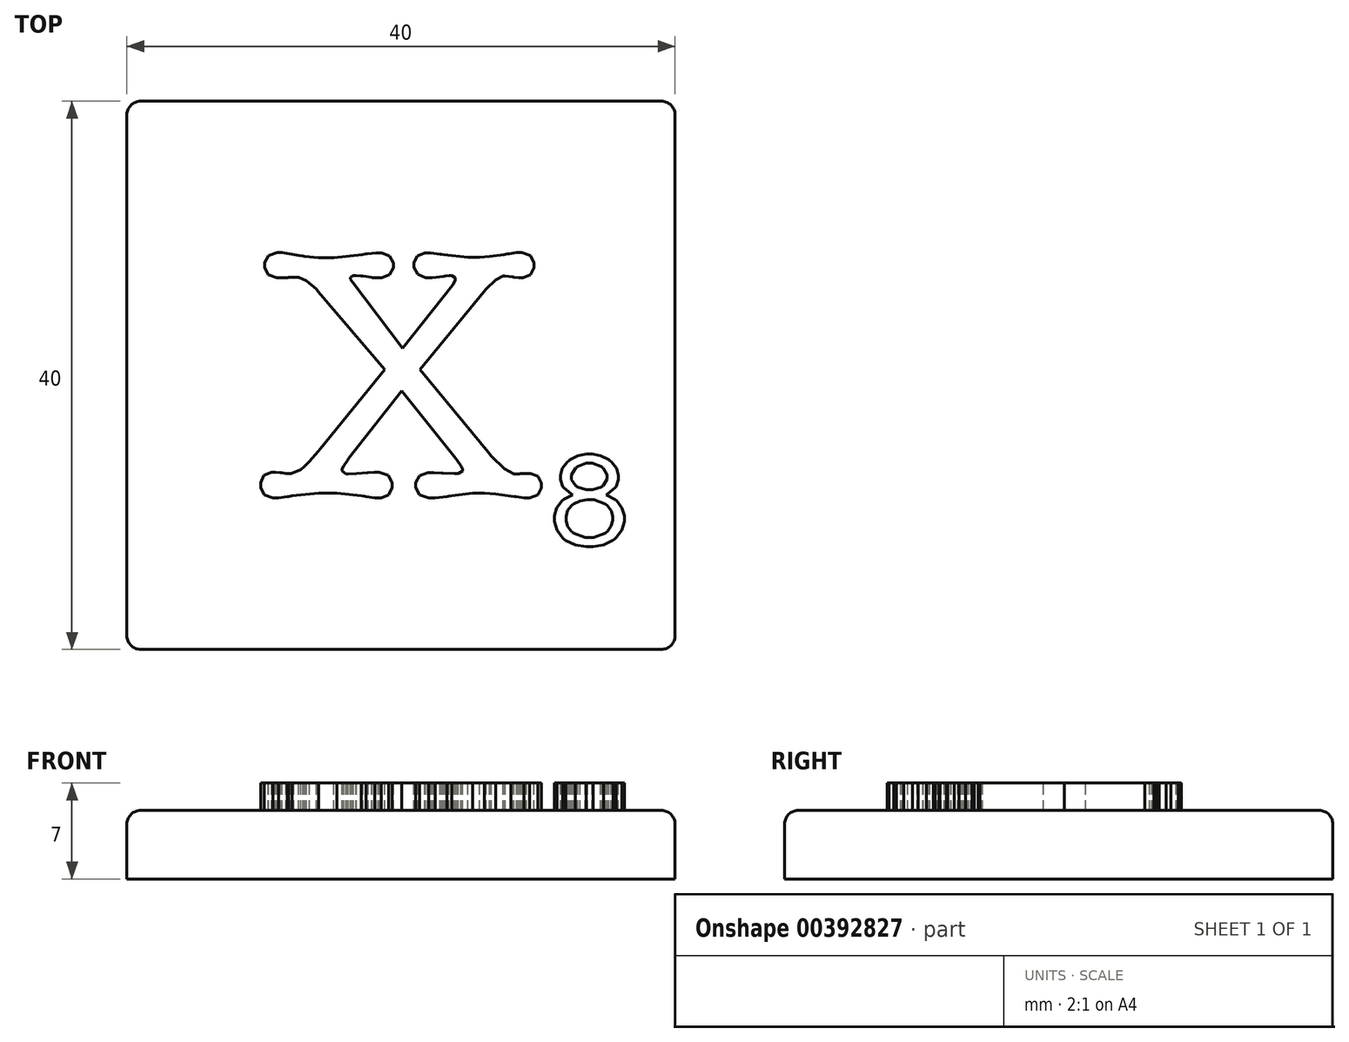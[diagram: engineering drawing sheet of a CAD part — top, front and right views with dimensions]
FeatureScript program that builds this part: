
annotation { "Feature Type Name" : "Feature", "Feature Type Description" : "" }
export const myFeature = defineFeature(function(context is Context, id is Id, definition is map)
    precondition{}
    {
        {
            var Q0;
            Q0=qCreatedBy(makeId("Top.planeOp"),FACE);
            var sketch = newSketch(context, id + "F0", { "sketchPlane" : qUnion([Q0])});
            skLineSegment(sketch, "E0.bottom", {"start": v(20, -20) * mm, "end": v(-20, -20) * mm});
            skLineSegment(sketch, "E0.top", {"start": v(20, 20) * mm, "end": v(-20, 20) * mm});
            skLineSegment(sketch, "E0.left", {"start": v(20, -20) * mm, "end": v(20, 20) * mm});
            skLineSegment(sketch, "E0.right", {"start": v(-20, -20) * mm, "end": v(-20, 20) * mm});
            skPoint(sketch, "E0.middle", {"position": v(0, 0) * mm});
            skSolve(sketch);
        }
        {
            var Q0;
            Q0=makeQuery(id+"F0.imprint","IMPRINT",FACE,{"disambiguationData":[TD([[makeQuery(id+"F0.imprint","IMPRINT",EDGE,{"derivedFrom":sQuery(id+"F0.wireOp",EDGE,"E0.bottom")}),-1.0]])]});
            extrude(context, id + "F1", {"entities" : qUnion([Q0]), "depth" : -5 * mm});
        }
        {
            var Q0;
            Q0=makeQuery(id+"F1.opExtrude","CAP_FACE",FACE,{"disambiguationData":[OSD([sQuery(id+"F0.wireOp",EDGE,"E0.bottom"),sQuery(id+"F0.wireOp",EDGE,"E0.top"),sQuery(id+"F0.wireOp",EDGE,"E0.left"),sQuery(id+"F0.wireOp",EDGE,"E0.right")])],"isStart":true});
            var Q1;
            Q1=makeQuery(id+"F1.opExtrude","SWEPT_EDGE",EDGE,{"disambiguationData":[OSD([sQuery(id+"F0.wireOp",EDGE,"E0.top"),sQuery(id+"F0.wireOp",EDGE,"E0.right")])]});
            var Q2;
            Q2=makeQuery(id+"F1.opExtrude","SWEPT_EDGE",EDGE,{"disambiguationData":[OSD([sQuery(id+"F0.wireOp",EDGE,"E0.top"),sQuery(id+"F0.wireOp",EDGE,"E0.left")])]});
            var Q3;
            Q3=makeQuery(id+"F1.opExtrude","SWEPT_EDGE",EDGE,{"disambiguationData":[OSD([sQuery(id+"F0.wireOp",EDGE,"E0.bottom"),sQuery(id+"F0.wireOp",EDGE,"E0.right")])]});
            var Q4;
            Q4=makeQuery(id+"F1.opExtrude","SWEPT_EDGE",EDGE,{"disambiguationData":[OSD([sQuery(id+"F0.wireOp",EDGE,"E0.bottom"),sQuery(id+"F0.wireOp",EDGE,"E0.left")])]});
            fillet(context, id + "F2", {"entities" : qUnion([Q0, Q1, Q2, Q3, Q4]), "radius" : 1 * mm, "tangentPropagation" : true, "allowEdgeOverflow" : false});
        }
        {
            var Q0;
            Q0=qCreatedBy(makeId("Top.planeOp"),FACE);
            var sketch = newSketch(context, id + "F3", { "sketchPlane" : qUnion([Q0])});
            skLineSegment(sketch, "E1", {"start": v(-5.87, -5.36) * mm, "end": v(-1.2, 0.41) * mm});
            skLineSegment(sketch, "E2", {"start": v(-1.2, 0.41) * mm, "end": v(-6.03, 6.1) * mm});
            skLineSegment(sketch, "E3", {"start": v(-6.03, 6.1) * mm, "end": v(-6.18, 6.28) * mm});
            skLineSegment(sketch, "E4", {"start": v(-6.18, 6.28) * mm, "end": v(-6.9, 6.9) * mm});
            skLineSegment(sketch, "E5", {"start": v(-6.9, 6.9) * mm, "end": v(-7.48, 7.16) * mm});
            skLineSegment(sketch, "E6", {"start": v(-7.48, 7.16) * mm, "end": v(-7.67, 7.16) * mm});
            skLineSegment(sketch, "E7", {"start": v(-7.67, 7.16) * mm, "end": v(-7.82, 7.16) * mm});
            skLineSegment(sketch, "E8", {"start": v(-7.82, 7.16) * mm, "end": v(-8.2, 7.14) * mm});
            skLineSegment(sketch, "E9", {"start": v(-8.2, 7.14) * mm, "end": v(-8.27, 7.13) * mm});
            skLineSegment(sketch, "E10", {"start": v(-8.27, 7.13) * mm, "end": v(-8.33, 7.13) * mm});
            skLineSegment(sketch, "E11", {"start": v(-8.33, 7.13) * mm, "end": v(-8.73, 7.1) * mm});
            skLineSegment(sketch, "E12", {"start": v(-8.73, 7.1) * mm, "end": v(-8.86, 7.1) * mm});
            skLineSegment(sketch, "E13", {"start": v(-8.86, 7.1) * mm, "end": v(-9.07, 7.1) * mm});
            skLineSegment(sketch, "E14", {"start": v(-9.07, 7.1) * mm, "end": v(-9.68, 7.34) * mm});
            skLineSegment(sketch, "E15", {"start": v(-9.68, 7.34) * mm, "end": v(-9.95, 7.88) * mm});
            skLineSegment(sketch, "E16", {"start": v(-9.95, 7.88) * mm, "end": v(-9.95, 8.06) * mm});
            skLineSegment(sketch, "E17", {"start": v(-9.95, 8.06) * mm, "end": v(-9.95, 8.23) * mm});
            skLineSegment(sketch, "E18", {"start": v(-9.95, 8.23) * mm, "end": v(-9.66, 8.73) * mm});
            skLineSegment(sketch, "E19", {"start": v(-9.66, 8.73) * mm, "end": v(-9.02, 8.96) * mm});
            skLineSegment(sketch, "E20", {"start": v(-9.02, 8.96) * mm, "end": v(-8.81, 8.96) * mm});
            skLineSegment(sketch, "E21", {"start": v(-8.81, 8.96) * mm, "end": v(-8.7, 8.96) * mm});
            skLineSegment(sketch, "E22", {"start": v(-8.7, 8.96) * mm, "end": v(-8.33, 8.89) * mm});
            skLineSegment(sketch, "E23", {"start": v(-8.33, 8.89) * mm, "end": v(-7.4, 8.74) * mm});
            skLineSegment(sketch, "E24", {"start": v(-7.4, 8.74) * mm, "end": v(-7.14, 8.7) * mm});
            skLineSegment(sketch, "E25", {"start": v(-7.14, 8.7) * mm, "end": v(-7.02, 8.67) * mm});
            skLineSegment(sketch, "E26", {"start": v(-7.02, 8.67) * mm, "end": v(-6, 8.59) * mm});
            skLineSegment(sketch, "E27", {"start": v(-6, 8.59) * mm, "end": v(-5.66, 8.59) * mm});
            skLineSegment(sketch, "E28", {"start": v(-5.66, 8.59) * mm, "end": v(-4.88, 8.59) * mm});
            skLineSegment(sketch, "E29", {"start": v(-4.88, 8.59) * mm, "end": v(-2.83, 8.8) * mm});
            skLineSegment(sketch, "E30", {"start": v(-2.83, 8.8) * mm, "end": v(-2.54, 8.85) * mm});
            skLineSegment(sketch, "E31", {"start": v(-2.54, 8.85) * mm, "end": v(-2.45, 8.86) * mm});
            skLineSegment(sketch, "E32", {"start": v(-2.45, 8.86) * mm, "end": v(-1.82, 8.93) * mm});
            skLineSegment(sketch, "E33", {"start": v(-1.82, 8.93) * mm, "end": v(-1.61, 8.93) * mm});
            skLineSegment(sketch, "E34", {"start": v(-1.61, 8.93) * mm, "end": v(-1.42, 8.93) * mm});
            skLineSegment(sketch, "E35", {"start": v(-1.42, 8.93) * mm, "end": v(-0.82, 8.7) * mm});
            skLineSegment(sketch, "E36", {"start": v(-0.82, 8.7) * mm, "end": v(-0.56, 8.2) * mm});
            skLineSegment(sketch, "E37", {"start": v(-0.56, 8.2) * mm, "end": v(-0.56, 8.03) * mm});
            skLineSegment(sketch, "E38", {"start": v(-0.56, 8.03) * mm, "end": v(-0.56, 7.86) * mm});
            skLineSegment(sketch, "E39", {"start": v(-0.56, 7.86) * mm, "end": v(-0.82, 7.34) * mm});
            skLineSegment(sketch, "E40", {"start": v(-0.82, 7.34) * mm, "end": v(-1.42, 7.1) * mm});
            skLineSegment(sketch, "E41", {"start": v(-1.42, 7.1) * mm, "end": v(-1.61, 7.1) * mm});
            skLineSegment(sketch, "E42", {"start": v(-1.61, 7.1) * mm, "end": v(-1.68, 7.1) * mm});
            skLineSegment(sketch, "E43", {"start": v(-1.68, 7.1) * mm, "end": v(-1.83, 7.13) * mm});
            skLineSegment(sketch, "E44", {"start": v(-1.83, 7.13) * mm, "end": v(-1.85, 7.13) * mm});
            skLineSegment(sketch, "E45", {"start": v(-1.85, 7.13) * mm, "end": v(-2.1, 7.13) * mm});
            skLineSegment(sketch, "E46", {"start": v(-2.1, 7.13) * mm, "end": v(-2.15, 7.14) * mm});
            skLineSegment(sketch, "E47", {"start": v(-2.15, 7.14) * mm, "end": v(-2.78, 7.23) * mm});
            skLineSegment(sketch, "E48", {"start": v(-2.78, 7.23) * mm, "end": v(-2.84, 7.24) * mm});
            skLineSegment(sketch, "E49", {"start": v(-2.84, 7.24) * mm, "end": v(-2.91, 7.25) * mm});
            skLineSegment(sketch, "E50", {"start": v(-2.91, 7.25) * mm, "end": v(-3.27, 7.29) * mm});
            skLineSegment(sketch, "E51", {"start": v(-3.27, 7.29) * mm, "end": v(-3.39, 7.29) * mm});
            skLineSegment(sketch, "E52", {"start": v(-3.39, 7.29) * mm, "end": v(-3.47, 7.29) * mm});
            skLineSegment(sketch, "E53", {"start": v(-3.47, 7.29) * mm, "end": v(-3.7, 7.15) * mm});
            skLineSegment(sketch, "E54", {"start": v(-3.7, 7.15) * mm, "end": v(-3.7, 7.1) * mm});
            skLineSegment(sketch, "E55", {"start": v(-3.7, 7.1) * mm, "end": v(-3.7, 7.03) * mm});
            skLineSegment(sketch, "E56", {"start": v(-3.7, 7.03) * mm, "end": v(-3.57, 6.82) * mm});
            skLineSegment(sketch, "E57", {"start": v(-3.57, 6.82) * mm, "end": v(-3.55, 6.79) * mm});
            skLineSegment(sketch, "E58", {"start": v(-3.55, 6.79) * mm, "end": v(0.13, 1.97) * mm});
            skLineSegment(sketch, "E59", {"start": v(0.13, 1.97) * mm, "end": v(3.76, 6.57) * mm});
            skLineSegment(sketch, "E60", {"start": v(3.76, 6.57) * mm, "end": v(3.8, 6.62) * mm});
            skLineSegment(sketch, "E61", {"start": v(3.8, 6.62) * mm, "end": v(3.97, 6.94) * mm});
            skLineSegment(sketch, "E62", {"start": v(3.97, 6.94) * mm, "end": v(3.97, 7.05) * mm});
            skLineSegment(sketch, "E63", {"start": v(3.97, 7.05) * mm, "end": v(3.97, 7.1) * mm});
            skLineSegment(sketch, "E64", {"start": v(3.97, 7.1) * mm, "end": v(3.71, 7.26) * mm});
            skLineSegment(sketch, "E65", {"start": v(3.71, 7.26) * mm, "end": v(3.62, 7.26) * mm});
            skLineSegment(sketch, "E66", {"start": v(3.62, 7.26) * mm, "end": v(3.53, 7.26) * mm});
            skLineSegment(sketch, "E67", {"start": v(3.53, 7.26) * mm, "end": v(3.26, 7.24) * mm});
            skLineSegment(sketch, "E68", {"start": v(3.26, 7.24) * mm, "end": v(3.23, 7.24) * mm});
            skLineSegment(sketch, "E69", {"start": v(3.23, 7.24) * mm, "end": v(3.1, 7.22) * mm});
            skLineSegment(sketch, "E70", {"start": v(3.1, 7.22) * mm, "end": v(2.28, 7.13) * mm});
            skLineSegment(sketch, "E71", {"start": v(2.28, 7.13) * mm, "end": v(2, 7.13) * mm});
            skLineSegment(sketch, "E72", {"start": v(2, 7.13) * mm, "end": v(1.81, 7.13) * mm});
            skLineSegment(sketch, "E73", {"start": v(1.81, 7.13) * mm, "end": v(1.22, 7.36) * mm});
            skLineSegment(sketch, "E74", {"start": v(1.22, 7.36) * mm, "end": v(0.95, 7.88) * mm});
            skLineSegment(sketch, "E75", {"start": v(0.95, 7.88) * mm, "end": v(0.95, 8.06) * mm});
            skLineSegment(sketch, "E76", {"start": v(0.95, 8.06) * mm, "end": v(0.95, 8.22) * mm});
            skLineSegment(sketch, "E77", {"start": v(0.95, 8.22) * mm, "end": v(1.2, 8.71) * mm});
            skLineSegment(sketch, "E78", {"start": v(1.2, 8.71) * mm, "end": v(1.75, 8.93) * mm});
            skLineSegment(sketch, "E79", {"start": v(1.75, 8.93) * mm, "end": v(1.93, 8.93) * mm});
            skLineSegment(sketch, "E80", {"start": v(1.93, 8.93) * mm, "end": v(2.18, 8.93) * mm});
            skLineSegment(sketch, "E81", {"start": v(2.18, 8.93) * mm, "end": v(2.83, 8.84) * mm});
            skLineSegment(sketch, "E82", {"start": v(2.83, 8.84) * mm, "end": v(2.94, 8.82) * mm});
            skLineSegment(sketch, "E83", {"start": v(2.94, 8.82) * mm, "end": v(3.14, 8.79) * mm});
            skLineSegment(sketch, "E84", {"start": v(3.14, 8.79) * mm, "end": v(4.9, 8.61) * mm});
            skLineSegment(sketch, "E85", {"start": v(4.9, 8.61) * mm, "end": v(5.48, 8.61) * mm});
            skLineSegment(sketch, "E86", {"start": v(5.48, 8.61) * mm, "end": v(5.72, 8.61) * mm});
            skLineSegment(sketch, "E87", {"start": v(5.72, 8.61) * mm, "end": v(6.46, 8.67) * mm});
            skLineSegment(sketch, "E88", {"start": v(6.46, 8.67) * mm, "end": v(7.53, 8.81) * mm});
            skLineSegment(sketch, "E89", {"start": v(7.53, 8.81) * mm, "end": v(7.78, 8.85) * mm});
            skLineSegment(sketch, "E90", {"start": v(7.78, 8.85) * mm, "end": v(7.89, 8.87) * mm});
            skLineSegment(sketch, "E91", {"start": v(7.89, 8.87) * mm, "end": v(8.44, 8.96) * mm});
            skLineSegment(sketch, "E92", {"start": v(8.44, 8.96) * mm, "end": v(8.62, 8.96) * mm});
            skLineSegment(sketch, "E93", {"start": v(8.62, 8.96) * mm, "end": v(8.83, 8.96) * mm});
            skLineSegment(sketch, "E94", {"start": v(8.83, 8.96) * mm, "end": v(9.44, 8.72) * mm});
            skLineSegment(sketch, "E95", {"start": v(9.44, 8.72) * mm, "end": v(9.71, 8.2) * mm});
            skLineSegment(sketch, "E96", {"start": v(9.71, 8.2) * mm, "end": v(9.71, 8.03) * mm});
            skLineSegment(sketch, "E97", {"start": v(9.71, 8.03) * mm, "end": v(9.71, 7.86) * mm});
            skLineSegment(sketch, "E98", {"start": v(9.71, 7.86) * mm, "end": v(9.47, 7.34) * mm});
            skLineSegment(sketch, "E99", {"start": v(9.47, 7.34) * mm, "end": v(8.91, 7.1) * mm});
            skLineSegment(sketch, "E100", {"start": v(8.91, 7.1) * mm, "end": v(8.73, 7.1) * mm});
            skLineSegment(sketch, "E101", {"start": v(8.73, 7.1) * mm, "end": v(8.6, 7.1) * mm});
            skLineSegment(sketch, "E102", {"start": v(8.6, 7.1) * mm, "end": v(8.24, 7.16) * mm});
            skLineSegment(sketch, "E103", {"start": v(8.24, 7.16) * mm, "end": v(8.18, 7.17) * mm});
            skLineSegment(sketch, "E104", {"start": v(8.18, 7.17) * mm, "end": v(8.11, 7.18) * mm});
            skLineSegment(sketch, "E105", {"start": v(8.11, 7.18) * mm, "end": v(7.62, 7.24) * mm});
            skLineSegment(sketch, "E106", {"start": v(7.62, 7.24) * mm, "end": v(7.44, 7.24) * mm});
            skLineSegment(sketch, "E107", {"start": v(7.44, 7.24) * mm, "end": v(6.91, 6.95) * mm});
            skLineSegment(sketch, "E108", {"start": v(6.91, 6.95) * mm, "end": v(6.21, 6.29) * mm});
            skLineSegment(sketch, "E109", {"start": v(6.21, 6.29) * mm, "end": v(6.06, 6.1) * mm});
            skLineSegment(sketch, "E110", {"start": v(6.06, 6.1) * mm, "end": v(1.4, 0.41) * mm});
            skLineSegment(sketch, "E111", {"start": v(1.4, 0.41) * mm, "end": v(6.38, -5.62) * mm});
            skLineSegment(sketch, "E112", {"start": v(6.38, -5.62) * mm, "end": v(6.6, -5.89) * mm});
            skLineSegment(sketch, "E113", {"start": v(6.6, -5.89) * mm, "end": v(7.55, -6.81) * mm});
            skLineSegment(sketch, "E114", {"start": v(7.55, -6.81) * mm, "end": v(8.26, -7.2) * mm});
            skLineSegment(sketch, "E115", {"start": v(8.26, -7.2) * mm, "end": v(8.5, -7.2) * mm});
            skLineSegment(sketch, "E116", {"start": v(8.5, -7.2) * mm, "end": v(8.54, -7.2) * mm});
            skLineSegment(sketch, "E117", {"start": v(8.54, -7.2) * mm, "end": v(8.66, -7.19) * mm});
            skLineSegment(sketch, "E118", {"start": v(8.66, -7.19) * mm, "end": v(8.68, -7.18) * mm});
            skLineSegment(sketch, "E119", {"start": v(8.68, -7.18) * mm, "end": v(8.84, -7.18) * mm});
            skLineSegment(sketch, "E120", {"start": v(8.84, -7.18) * mm, "end": v(8.86, -7.18) * mm});
            skLineSegment(sketch, "E121", {"start": v(8.86, -7.18) * mm, "end": v(9.16, -7.16) * mm});
            skLineSegment(sketch, "E122", {"start": v(9.16, -7.16) * mm, "end": v(9.26, -7.16) * mm});
            skLineSegment(sketch, "E123", {"start": v(9.26, -7.16) * mm, "end": v(9.44, -7.16) * mm});
            skLineSegment(sketch, "E124", {"start": v(9.44, -7.16) * mm, "end": v(10, -7.37) * mm});
            skLineSegment(sketch, "E125", {"start": v(10, -7.37) * mm, "end": v(10.24, -7.87) * mm});
            skLineSegment(sketch, "E126", {"start": v(10.24, -7.87) * mm, "end": v(10.24, -8.03) * mm});
            skLineSegment(sketch, "E127", {"start": v(10.24, -8.03) * mm, "end": v(10.24, -8.2) * mm});
            skLineSegment(sketch, "E128", {"start": v(10.24, -8.2) * mm, "end": v(9.98, -8.72) * mm});
            skLineSegment(sketch, "E129", {"start": v(9.98, -8.72) * mm, "end": v(9.4, -8.96) * mm});
            skLineSegment(sketch, "E130", {"start": v(9.4, -8.96) * mm, "end": v(9.2, -8.96) * mm});
            skLineSegment(sketch, "E131", {"start": v(9.2, -8.96) * mm, "end": v(8.98, -8.96) * mm});
            skLineSegment(sketch, "E132", {"start": v(8.98, -8.96) * mm, "end": v(8.4, -8.87) * mm});
            skLineSegment(sketch, "E133", {"start": v(8.4, -8.87) * mm, "end": v(8.28, -8.85) * mm});
            skLineSegment(sketch, "E134", {"start": v(8.28, -8.85) * mm, "end": v(8.03, -8.8) * mm});
            skLineSegment(sketch, "E135", {"start": v(8.03, -8.8) * mm, "end": v(6.91, -8.67) * mm});
            skLineSegment(sketch, "E136", {"start": v(6.91, -8.67) * mm, "end": v(6.1, -8.61) * mm});
            skLineSegment(sketch, "E137", {"start": v(6.1, -8.61) * mm, "end": v(5.82, -8.61) * mm});
            skLineSegment(sketch, "E138", {"start": v(5.82, -8.61) * mm, "end": v(5.24, -8.61) * mm});
            skLineSegment(sketch, "E139", {"start": v(5.24, -8.61) * mm, "end": v(3.7, -8.79) * mm});
            skLineSegment(sketch, "E140", {"start": v(3.7, -8.79) * mm, "end": v(3.5, -8.82) * mm});
            skLineSegment(sketch, "E141", {"start": v(3.5, -8.82) * mm, "end": v(3.36, -8.85) * mm});
            skLineSegment(sketch, "E142", {"start": v(3.36, -8.85) * mm, "end": v(2.5, -8.96) * mm});
            skLineSegment(sketch, "E143", {"start": v(2.5, -8.96) * mm, "end": v(2.22, -8.96) * mm});
            skLineSegment(sketch, "E144", {"start": v(2.22, -8.96) * mm, "end": v(2, -8.96) * mm});
            skLineSegment(sketch, "E145", {"start": v(2, -8.96) * mm, "end": v(1.37, -8.72) * mm});
            skLineSegment(sketch, "E146", {"start": v(1.37, -8.72) * mm, "end": v(1.08, -8.18) * mm});
            skLineSegment(sketch, "E147", {"start": v(1.08, -8.18) * mm, "end": v(1.08, -8) * mm});
            skLineSegment(sketch, "E148", {"start": v(1.08, -8) * mm, "end": v(1.08, -7.83) * mm});
            skLineSegment(sketch, "E149", {"start": v(1.08, -7.83) * mm, "end": v(1.36, -7.33) * mm});
            skLineSegment(sketch, "E150", {"start": v(1.36, -7.33) * mm, "end": v(1.97, -7.1) * mm});
            skLineSegment(sketch, "E151", {"start": v(1.97, -7.1) * mm, "end": v(2.17, -7.1) * mm});
            skLineSegment(sketch, "E152", {"start": v(2.17, -7.1) * mm, "end": v(2.4, -7.1) * mm});
            skLineSegment(sketch, "E153", {"start": v(2.4, -7.1) * mm, "end": v(3, -7.12) * mm});
            skLineSegment(sketch, "E154", {"start": v(3, -7.12) * mm, "end": v(3.07, -7.13) * mm});
            skLineSegment(sketch, "E155", {"start": v(3.07, -7.13) * mm, "end": v(3.89, -7.18) * mm});
            skLineSegment(sketch, "E156", {"start": v(3.89, -7.18) * mm, "end": v(4.07, -7.18) * mm});
            skLineSegment(sketch, "E157", {"start": v(4.07, -7.18) * mm, "end": v(4.18, -7.18) * mm});
            skLineSegment(sketch, "E158", {"start": v(4.18, -7.18) * mm, "end": v(4.5, -6.99) * mm});
            skLineSegment(sketch, "E159", {"start": v(4.5, -6.99) * mm, "end": v(4.5, -6.92) * mm});
            skLineSegment(sketch, "E160", {"start": v(4.5, -6.92) * mm, "end": v(4.5, -6.84) * mm});
            skLineSegment(sketch, "E161", {"start": v(4.5, -6.84) * mm, "end": v(4.37, -6.6) * mm});
            skLineSegment(sketch, "E162", {"start": v(4.37, -6.6) * mm, "end": v(4.08, -6.18) * mm});
            skLineSegment(sketch, "E163", {"start": v(4.08, -6.18) * mm, "end": v(4, -6.07) * mm});
            skLineSegment(sketch, "E164", {"start": v(4, -6.07) * mm, "end": v(0.05, -1.12) * mm});
            skLineSegment(sketch, "E165", {"start": v(0.05, -1.12) * mm, "end": v(-3.81, -6.07) * mm});
            skLineSegment(sketch, "E166", {"start": v(-3.81, -6.07) * mm, "end": v(-3.9, -6.17) * mm});
            skLineSegment(sketch, "E167", {"start": v(-3.9, -6.17) * mm, "end": v(-4.17, -6.59) * mm});
            skLineSegment(sketch, "E168", {"start": v(-4.17, -6.59) * mm, "end": v(-4.29, -6.84) * mm});
            skLineSegment(sketch, "E169", {"start": v(-4.29, -6.84) * mm, "end": v(-4.29, -6.92) * mm});
            skLineSegment(sketch, "E170", {"start": v(-4.29, -6.92) * mm, "end": v(-4.29, -7) * mm});
            skLineSegment(sketch, "E171", {"start": v(-4.29, -7) * mm, "end": v(-4, -7.2) * mm});
            skLineSegment(sketch, "E172", {"start": v(-4, -7.2) * mm, "end": v(-3.92, -7.2) * mm});
            skLineSegment(sketch, "E173", {"start": v(-3.92, -7.2) * mm, "end": v(-3.86, -7.2) * mm});
            skLineSegment(sketch, "E174", {"start": v(-3.86, -7.2) * mm, "end": v(-3.25, -7.16) * mm});
            skLineSegment(sketch, "E175", {"start": v(-3.25, -7.16) * mm, "end": v(-2.46, -7.1) * mm});
            skLineSegment(sketch, "E176", {"start": v(-2.46, -7.1) * mm, "end": v(-2.4, -7.1) * mm});
            skLineSegment(sketch, "E177", {"start": v(-2.4, -7.1) * mm, "end": v(-1.95, -7.08) * mm});
            skLineSegment(sketch, "E178", {"start": v(-1.95, -7.08) * mm, "end": v(-1.8, -7.08) * mm});
            skLineSegment(sketch, "E179", {"start": v(-1.8, -7.08) * mm, "end": v(-1.58, -7.08) * mm});
            skLineSegment(sketch, "E180", {"start": v(-1.58, -7.08) * mm, "end": v(-0.93, -7.3) * mm});
            skLineSegment(sketch, "E181", {"start": v(-0.93, -7.3) * mm, "end": v(-0.64, -7.83) * mm});
            skLineSegment(sketch, "E182", {"start": v(-0.64, -7.83) * mm, "end": v(-0.64, -8) * mm});
            skLineSegment(sketch, "E183", {"start": v(-0.64, -8) * mm, "end": v(-0.64, -8.18) * mm});
            skLineSegment(sketch, "E184", {"start": v(-0.64, -8.18) * mm, "end": v(-0.89, -8.72) * mm});
            skLineSegment(sketch, "E185", {"start": v(-0.89, -8.72) * mm, "end": v(-1.45, -8.96) * mm});
            skLineSegment(sketch, "E186", {"start": v(-1.45, -8.96) * mm, "end": v(-1.64, -8.96) * mm});
            skLineSegment(sketch, "E187", {"start": v(-1.64, -8.96) * mm, "end": v(-1.9, -8.96) * mm});
            skLineSegment(sketch, "E188", {"start": v(-1.9, -8.96) * mm, "end": v(-2.55, -8.85) * mm});
            skLineSegment(sketch, "E189", {"start": v(-2.55, -8.85) * mm, "end": v(-2.67, -8.82) * mm});
            skLineSegment(sketch, "E190", {"start": v(-2.67, -8.82) * mm, "end": v(-2.89, -8.78) * mm});
            skLineSegment(sketch, "E191", {"start": v(-2.89, -8.78) * mm, "end": v(-4.67, -8.59) * mm});
            skLineSegment(sketch, "E192", {"start": v(-4.67, -8.59) * mm, "end": v(-5.27, -8.59) * mm});
            skLineSegment(sketch, "E193", {"start": v(-5.27, -8.59) * mm, "end": v(-6, -8.59) * mm});
            skLineSegment(sketch, "E194", {"start": v(-6, -8.59) * mm, "end": v(-7.96, -8.8) * mm});
            skLineSegment(sketch, "E195", {"start": v(-7.96, -8.8) * mm, "end": v(-8.2, -8.85) * mm});
            skLineSegment(sketch, "E196", {"start": v(-8.2, -8.85) * mm, "end": v(-8.3, -8.87) * mm});
            skLineSegment(sketch, "E197", {"start": v(-8.3, -8.87) * mm, "end": v(-8.92, -8.96) * mm});
            skLineSegment(sketch, "E198", {"start": v(-8.92, -8.96) * mm, "end": v(-9.13, -8.96) * mm});
            skLineSegment(sketch, "E199", {"start": v(-9.13, -8.96) * mm, "end": v(-9.34, -8.96) * mm});
            skLineSegment(sketch, "E200", {"start": v(-9.34, -8.96) * mm, "end": v(-9.96, -8.72) * mm});
            skLineSegment(sketch, "E201", {"start": v(-9.96, -8.72) * mm, "end": v(-10.24, -8.18) * mm});
            skLineSegment(sketch, "E202", {"start": v(-10.24, -8.18) * mm, "end": v(-10.24, -8) * mm});
            skLineSegment(sketch, "E203", {"start": v(-10.24, -8) * mm, "end": v(-10.24, -7.83) * mm});
            skLineSegment(sketch, "E204", {"start": v(-10.24, -7.83) * mm, "end": v(-10, -7.3) * mm});
            skLineSegment(sketch, "E205", {"start": v(-10, -7.3) * mm, "end": v(-9.45, -7.08) * mm});
            skLineSegment(sketch, "E206", {"start": v(-9.45, -7.08) * mm, "end": v(-9.26, -7.08) * mm});
            skLineSegment(sketch, "E207", {"start": v(-9.26, -7.08) * mm, "end": v(-9.14, -7.08) * mm});
            skLineSegment(sketch, "E208", {"start": v(-9.14, -7.08) * mm, "end": v(-8.83, -7.11) * mm});
            skLineSegment(sketch, "E209", {"start": v(-8.83, -7.11) * mm, "end": v(-8.77, -7.12) * mm});
            skLineSegment(sketch, "E210", {"start": v(-8.77, -7.12) * mm, "end": v(-8.72, -7.12) * mm});
            skLineSegment(sketch, "E211", {"start": v(-8.72, -7.12) * mm, "end": v(-8.4, -7.16) * mm});
            skLineSegment(sketch, "E212", {"start": v(-8.4, -7.16) * mm, "end": v(-8.28, -7.16) * mm});
            skLineSegment(sketch, "E213", {"start": v(-8.28, -7.16) * mm, "end": v(-8.02, -7.16) * mm});
            skLineSegment(sketch, "E214", {"start": v(-8.02, -7.16) * mm, "end": v(-7.3, -6.88) * mm});
            skLineSegment(sketch, "E215", {"start": v(-7.3, -6.88) * mm, "end": v(-7.24, -6.83) * mm});
            skLineSegment(sketch, "E216", {"start": v(-7.24, -6.83) * mm, "end": v(-7.17, -6.77) * mm});
            skLineSegment(sketch, "E217", {"start": v(-7.17, -6.77) * mm, "end": v(-6.68, -6.3) * mm});
            skLineSegment(sketch, "E218", {"start": v(-6.68, -6.3) * mm, "end": v(-6.03, -5.55) * mm});
            skLineSegment(sketch, "E219", {"start": v(-6.03, -5.55) * mm, "end": v(-5.87, -5.36) * mm});
            skSolve(sketch);
        }
        {
            var Q0;
            Q0=qCreatedBy(makeId("Top.planeOp"),FACE);
            var sketch = newSketch(context, id + "F4", { "sketchPlane" : qUnion([Q0])});
            skLineSegment(sketch, "E220", {"start": v(11.87, -9.06) * mm, "end": v(11.9, -9.03) * mm});
            skLineSegment(sketch, "E221", {"start": v(11.9, -9.03) * mm, "end": v(12.46, -8.74) * mm});
            skLineSegment(sketch, "E222", {"start": v(12.46, -8.74) * mm, "end": v(12.53, -8.72) * mm});
            skLineSegment(sketch, "E223", {"start": v(12.53, -8.72) * mm, "end": v(12.45, -8.67) * mm});
            skLineSegment(sketch, "E224", {"start": v(12.45, -8.67) * mm, "end": v(11.85, -8.2) * mm});
            skLineSegment(sketch, "E225", {"start": v(11.85, -8.2) * mm, "end": v(11.82, -8.15) * mm});
            skLineSegment(sketch, "E226", {"start": v(11.82, -8.15) * mm, "end": v(11.79, -8.1) * mm});
            skLineSegment(sketch, "E227", {"start": v(11.79, -8.1) * mm, "end": v(11.63, -7.62) * mm});
            skLineSegment(sketch, "E228", {"start": v(11.63, -7.62) * mm, "end": v(11.63, -7.45) * mm});
            skLineSegment(sketch, "E229", {"start": v(11.63, -7.45) * mm, "end": v(11.63, -7.29) * mm});
            skLineSegment(sketch, "E230", {"start": v(11.63, -7.29) * mm, "end": v(11.78, -6.79) * mm});
            skLineSegment(sketch, "E231", {"start": v(11.78, -6.79) * mm, "end": v(12.14, -6.32) * mm});
            skLineSegment(sketch, "E232", {"start": v(12.14, -6.32) * mm, "end": v(12.24, -6.24) * mm});
            skLineSegment(sketch, "E233", {"start": v(12.24, -6.24) * mm, "end": v(12.35, -6.16) * mm});
            skLineSegment(sketch, "E234", {"start": v(12.35, -6.16) * mm, "end": v(12.93, -5.87) * mm});
            skLineSegment(sketch, "E235", {"start": v(12.93, -5.87) * mm, "end": v(13.55, -5.75) * mm});
            skLineSegment(sketch, "E236", {"start": v(13.55, -5.75) * mm, "end": v(13.75, -5.75) * mm});
            skLineSegment(sketch, "E237", {"start": v(13.75, -5.75) * mm, "end": v(13.96, -5.75) * mm});
            skLineSegment(sketch, "E238", {"start": v(13.96, -5.75) * mm, "end": v(14.58, -5.87) * mm});
            skLineSegment(sketch, "E239", {"start": v(14.58, -5.87) * mm, "end": v(15.16, -6.16) * mm});
            skLineSegment(sketch, "E240", {"start": v(15.16, -6.16) * mm, "end": v(15.26, -6.24) * mm});
            skLineSegment(sketch, "E241", {"start": v(15.26, -6.24) * mm, "end": v(15.37, -6.32) * mm});
            skLineSegment(sketch, "E242", {"start": v(15.37, -6.32) * mm, "end": v(15.72, -6.79) * mm});
            skLineSegment(sketch, "E243", {"start": v(15.72, -6.79) * mm, "end": v(15.88, -7.29) * mm});
            skLineSegment(sketch, "E244", {"start": v(15.88, -7.29) * mm, "end": v(15.88, -7.45) * mm});
            skLineSegment(sketch, "E245", {"start": v(15.88, -7.45) * mm, "end": v(15.88, -7.63) * mm});
            skLineSegment(sketch, "E246", {"start": v(15.88, -7.63) * mm, "end": v(15.72, -8.1) * mm});
            skLineSegment(sketch, "E247", {"start": v(15.72, -8.1) * mm, "end": v(15.68, -8.15) * mm});
            skLineSegment(sketch, "E248", {"start": v(15.68, -8.15) * mm, "end": v(15.65, -8.2) * mm});
            skLineSegment(sketch, "E249", {"start": v(15.65, -8.2) * mm, "end": v(15.06, -8.67) * mm});
            skLineSegment(sketch, "E250", {"start": v(15.06, -8.67) * mm, "end": v(14.97, -8.72) * mm});
            skLineSegment(sketch, "E251", {"start": v(14.97, -8.72) * mm, "end": v(15.04, -8.74) * mm});
            skLineSegment(sketch, "E252", {"start": v(15.04, -8.74) * mm, "end": v(15.59, -9.03) * mm});
            skLineSegment(sketch, "E253", {"start": v(15.59, -9.03) * mm, "end": v(15.63, -9.06) * mm});
            skLineSegment(sketch, "E254", {"start": v(15.63, -9.06) * mm, "end": v(15.74, -9.15) * mm});
            skLineSegment(sketch, "E255", {"start": v(15.74, -9.15) * mm, "end": v(16.13, -9.67) * mm});
            skLineSegment(sketch, "E256", {"start": v(16.13, -9.67) * mm, "end": v(16.3, -10.26) * mm});
            skLineSegment(sketch, "E257", {"start": v(16.3, -10.26) * mm, "end": v(16.3, -10.46) * mm});
            skLineSegment(sketch, "E258", {"start": v(16.3, -10.46) * mm, "end": v(16.3, -10.67) * mm});
            skLineSegment(sketch, "E259", {"start": v(16.3, -10.67) * mm, "end": v(16.12, -11.3) * mm});
            skLineSegment(sketch, "E260", {"start": v(16.12, -11.3) * mm, "end": v(15.72, -11.85) * mm});
            skLineSegment(sketch, "E261", {"start": v(15.72, -11.85) * mm, "end": v(15.6, -11.95) * mm});
            skLineSegment(sketch, "E262", {"start": v(15.6, -11.95) * mm, "end": v(15.49, -12.04) * mm});
            skLineSegment(sketch, "E263", {"start": v(15.49, -12.04) * mm, "end": v(14.8, -12.38) * mm});
            skLineSegment(sketch, "E264", {"start": v(14.8, -12.38) * mm, "end": v(14.04, -12.52) * mm});
            skLineSegment(sketch, "E265", {"start": v(14.04, -12.52) * mm, "end": v(13.78, -12.52) * mm});
            skLineSegment(sketch, "E266", {"start": v(13.78, -12.52) * mm, "end": v(13.52, -12.52) * mm});
            skLineSegment(sketch, "E267", {"start": v(13.52, -12.52) * mm, "end": v(12.73, -12.38) * mm});
            skLineSegment(sketch, "E268", {"start": v(12.73, -12.38) * mm, "end": v(12.02, -12.05) * mm});
            skLineSegment(sketch, "E269", {"start": v(12.02, -12.05) * mm, "end": v(11.9, -11.96) * mm});
            skLineSegment(sketch, "E270", {"start": v(11.9, -11.96) * mm, "end": v(11.79, -11.86) * mm});
            skLineSegment(sketch, "E271", {"start": v(11.79, -11.86) * mm, "end": v(11.38, -11.3) * mm});
            skLineSegment(sketch, "E272", {"start": v(11.38, -11.3) * mm, "end": v(11.2, -10.67) * mm});
            skLineSegment(sketch, "E273", {"start": v(11.2, -10.67) * mm, "end": v(11.2, -10.46) * mm});
            skLineSegment(sketch, "E274", {"start": v(11.2, -10.46) * mm, "end": v(11.2, -10.26) * mm});
            skLineSegment(sketch, "E275", {"start": v(11.2, -10.26) * mm, "end": v(11.37, -9.67) * mm});
            skLineSegment(sketch, "E276", {"start": v(11.37, -9.67) * mm, "end": v(11.76, -9.15) * mm});
            skLineSegment(sketch, "E277", {"start": v(11.76, -9.15) * mm, "end": v(11.87, -9.06) * mm});
            skLineSegment(sketch, "E278", {"start": v(13.75, -6.42) * mm, "end": v(13.52, -6.42) * mm});
            skLineSegment(sketch, "E279", {"start": v(13.52, -6.42) * mm, "end": v(12.88, -6.67) * mm});
            skLineSegment(sketch, "E280", {"start": v(12.88, -6.67) * mm, "end": v(12.82, -6.72) * mm});
            skLineSegment(sketch, "E281", {"start": v(12.82, -6.72) * mm, "end": v(12.75, -6.76) * mm});
            skLineSegment(sketch, "E282", {"start": v(12.75, -6.76) * mm, "end": v(12.45, -7.28) * mm});
            skLineSegment(sketch, "E283", {"start": v(12.45, -7.28) * mm, "end": v(12.45, -7.45) * mm});
            skLineSegment(sketch, "E284", {"start": v(12.45, -7.45) * mm, "end": v(12.45, -7.62) * mm});
            skLineSegment(sketch, "E285", {"start": v(12.45, -7.62) * mm, "end": v(12.75, -8.06) * mm});
            skLineSegment(sketch, "E286", {"start": v(12.75, -8.06) * mm, "end": v(12.81, -8.1) * mm});
            skLineSegment(sketch, "E287", {"start": v(12.81, -8.1) * mm, "end": v(12.87, -8.15) * mm});
            skLineSegment(sketch, "E288", {"start": v(12.87, -8.15) * mm, "end": v(13.53, -8.36) * mm});
            skLineSegment(sketch, "E289", {"start": v(13.53, -8.36) * mm, "end": v(13.75, -8.36) * mm});
            skLineSegment(sketch, "E290", {"start": v(13.75, -8.36) * mm, "end": v(13.99, -8.36) * mm});
            skLineSegment(sketch, "E291", {"start": v(13.99, -8.36) * mm, "end": v(14.63, -8.15) * mm});
            skLineSegment(sketch, "E292", {"start": v(14.63, -8.15) * mm, "end": v(14.7, -8.1) * mm});
            skLineSegment(sketch, "E293", {"start": v(14.7, -8.1) * mm, "end": v(14.75, -8.06) * mm});
            skLineSegment(sketch, "E294", {"start": v(14.75, -8.06) * mm, "end": v(15.05, -7.6) * mm});
            skLineSegment(sketch, "E295", {"start": v(15.05, -7.6) * mm, "end": v(15.05, -7.44) * mm});
            skLineSegment(sketch, "E296", {"start": v(15.05, -7.44) * mm, "end": v(15.05, -7.26) * mm});
            skLineSegment(sketch, "E297", {"start": v(15.05, -7.26) * mm, "end": v(14.74, -6.76) * mm});
            skLineSegment(sketch, "E298", {"start": v(14.74, -6.76) * mm, "end": v(14.68, -6.71) * mm});
            skLineSegment(sketch, "E299", {"start": v(14.68, -6.71) * mm, "end": v(14.62, -6.66) * mm});
            skLineSegment(sketch, "E300", {"start": v(14.62, -6.66) * mm, "end": v(13.97, -6.42) * mm});
            skLineSegment(sketch, "E301", {"start": v(13.97, -6.42) * mm, "end": v(13.75, -6.42) * mm});
            skLineSegment(sketch, "E302", {"start": v(13.8, -9.08) * mm, "end": v(13.6, -9.08) * mm});
            skLineSegment(sketch, "E303", {"start": v(13.6, -9.08) * mm, "end": v(13.06, -9.17) * mm});
            skLineSegment(sketch, "E304", {"start": v(13.06, -9.17) * mm, "end": v(12.59, -9.39) * mm});
            skLineSegment(sketch, "E305", {"start": v(12.59, -9.39) * mm, "end": v(12.51, -9.45) * mm});
            skLineSegment(sketch, "E306", {"start": v(12.51, -9.45) * mm, "end": v(12.43, -9.5) * mm});
            skLineSegment(sketch, "E307", {"start": v(12.43, -9.5) * mm, "end": v(12.16, -9.88) * mm});
            skLineSegment(sketch, "E308", {"start": v(12.16, -9.88) * mm, "end": v(12.05, -10.31) * mm});
            skLineSegment(sketch, "E309", {"start": v(12.05, -10.31) * mm, "end": v(12.05, -10.45) * mm});
            skLineSegment(sketch, "E310", {"start": v(12.05, -10.45) * mm, "end": v(12.05, -10.6) * mm});
            skLineSegment(sketch, "E311", {"start": v(12.05, -10.6) * mm, "end": v(12.17, -11.01) * mm});
            skLineSegment(sketch, "E312", {"start": v(12.17, -11.01) * mm, "end": v(12.44, -11.4) * mm});
            skLineSegment(sketch, "E313", {"start": v(12.44, -11.4) * mm, "end": v(12.52, -11.46) * mm});
            skLineSegment(sketch, "E314", {"start": v(12.52, -11.46) * mm, "end": v(12.6, -11.52) * mm});
            skLineSegment(sketch, "E315", {"start": v(12.6, -11.52) * mm, "end": v(13.46, -11.84) * mm});
            skLineSegment(sketch, "E316", {"start": v(13.46, -11.84) * mm, "end": v(13.75, -11.84) * mm});
            skLineSegment(sketch, "E317", {"start": v(13.75, -11.84) * mm, "end": v(14.06, -11.84) * mm});
            skLineSegment(sketch, "E318", {"start": v(14.06, -11.84) * mm, "end": v(14.9, -11.52) * mm});
            skLineSegment(sketch, "E319", {"start": v(14.9, -11.52) * mm, "end": v(14.99, -11.46) * mm});
            skLineSegment(sketch, "E320", {"start": v(14.99, -11.46) * mm, "end": v(15.07, -11.4) * mm});
            skLineSegment(sketch, "E321", {"start": v(15.07, -11.4) * mm, "end": v(15.34, -11.01) * mm});
            skLineSegment(sketch, "E322", {"start": v(15.34, -11.01) * mm, "end": v(15.46, -10.6) * mm});
            skLineSegment(sketch, "E323", {"start": v(15.46, -10.6) * mm, "end": v(15.46, -10.45) * mm});
            skLineSegment(sketch, "E324", {"start": v(15.46, -10.45) * mm, "end": v(15.46, -10.31) * mm});
            skLineSegment(sketch, "E325", {"start": v(15.46, -10.31) * mm, "end": v(15.34, -9.9) * mm});
            skLineSegment(sketch, "E326", {"start": v(15.34, -9.9) * mm, "end": v(15.08, -9.52) * mm});
            skLineSegment(sketch, "E327", {"start": v(15.08, -9.52) * mm, "end": v(15, -9.46) * mm});
            skLineSegment(sketch, "E328", {"start": v(15, -9.46) * mm, "end": v(14.92, -9.4) * mm});
            skLineSegment(sketch, "E329", {"start": v(14.92, -9.4) * mm, "end": v(14.08, -9.08) * mm});
            skLineSegment(sketch, "E330", {"start": v(14.08, -9.08) * mm, "end": v(13.8, -9.08) * mm});
            skSolve(sketch);
        }
        {
            var Q0;
            Q0 = qSketchRegion(id + "F3", true);
            var Q1;
            Q1 = qSketchRegion(id + "F4", true);
            extrude(context, id + "F5", {"entities" : qUnion([Q0, Q1]), "operationType" : NewBodyOperationType.REMOVE, "oppositeDirection" : true, "depth" : 1 * mm});
        }
        {
            var Q0;
            Q0=qSketchRegion(id+"F3",true);
            var Q1;
            Q1=qSketchRegion(id+"F4",true);
            extrude(context, id + "F6", {"entities" : qUnion([Q0, Q1]), "depth" : -1 * mm});
        }
        {
            var Q0;
            Q0 = qSketchRegion(id + "F3", true);
            var Q1;
            Q1 = qSketchRegion(id + "F4", true);
            extrude(context, id + "F7", {"entities" : qUnion([Q0, Q1]), "operationType" : NewBodyOperationType.ADD, "depth" : 2 * mm});
        }
    });
